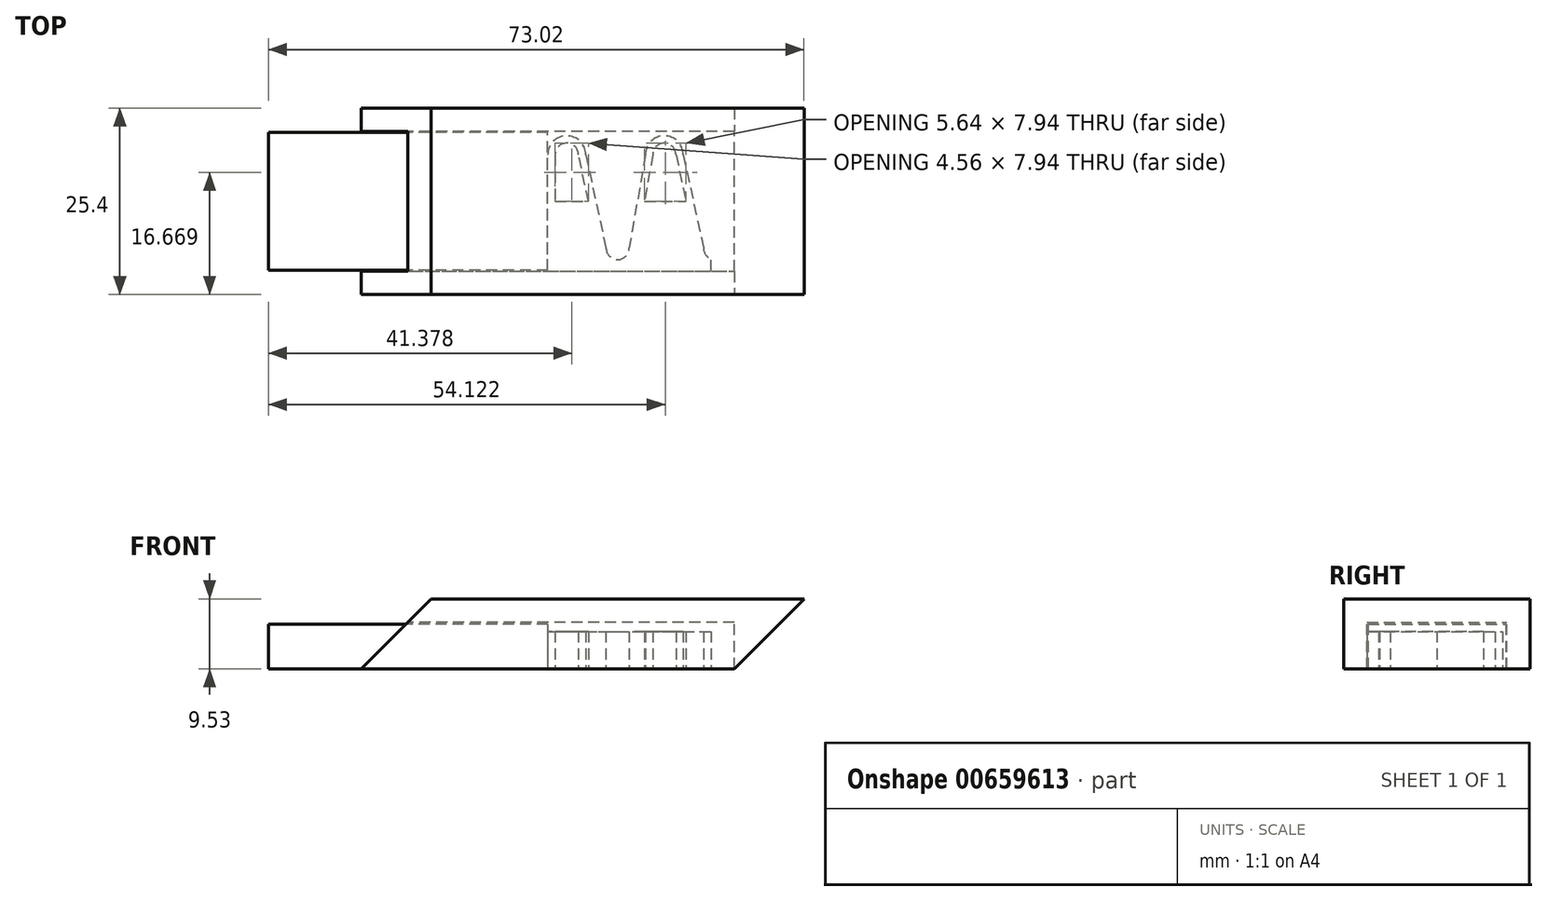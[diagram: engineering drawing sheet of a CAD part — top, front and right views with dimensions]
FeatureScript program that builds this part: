
annotation { "Feature Type Name" : "Feature", "Feature Type Description" : "" }
export const myFeature = defineFeature(function(context is Context, id is Id, definition is map)
    precondition{}
    {
        {
            var Q0;
            Q0=qCreatedBy(makeId("Top.planeOp"),FACE);
            var sketch = newSketch(context, id + "F0", { "sketchPlane" : qUnion([Q0])});
            skLineSegment(sketch, "E0.bottom", {"start": v(25.4, -12.7) * mm, "end": v(-25.4, -12.7) * mm});
            skLineSegment(sketch, "E0.top", {"start": v(25.4, 12.7) * mm, "end": v(-25.4, 12.7) * mm});
            skLineSegment(sketch, "E0.left", {"start": v(25.4, -12.7) * mm, "end": v(25.4, 12.7) * mm});
            skLineSegment(sketch, "E0.right", {"start": v(-25.4, -12.7) * mm, "end": v(-25.4, 12.7) * mm});
            skPoint(sketch, "E0.middle", {"position": v(0, 0) * mm});
            skLineSegment(sketch, "E1", {"start": v(25.4, 9.52) * mm, "end": v(-25.4, 9.52) * mm});
            skLineSegment(sketch, "E2", {"start": v(-25.4, -9.53) * mm, "end": v(25.4, -9.52) * mm});
            skSolve(sketch);
        }
        {
            var Q0;
            {var subQ0=sQuery(id+"F0.wireOp",EDGE,"E0.bottom");Q0=makeQuery(id+"F0.imprint","IMPRINT",FACE,{"disambiguationData":[TD([[makeQuery(id+"F0.imprint","IMPRINT",EDGE,{"derivedFrom":subQ0}),-1.0]])]});}
            var Q1;
            {var subQ0=sQuery(id+"F0.wireOp",EDGE,"E0.top");Q1=makeQuery(id+"F0.imprint","IMPRINT",FACE,{"disambiguationData":[TD([[makeQuery(id+"F0.imprint","IMPRINT",EDGE,{"derivedFrom":subQ0}),1.0]])]});}
            extrude(context, id + "F1", {"entities" : qUnion([Q0, Q1]), "depth" : 6.35 * mm, "offsetDistance" : 25.4 * mm});
        }
        {
            var Q0;
            Q0=makeQuery(id+"F1.opExtrude","SWEPT_FACE",FACE,{"disambiguationData":[OSD([sQuery(id+"F0.wireOp",EDGE,"E1")])]});
            var sketch = newSketch(context, id + "F2", { "sketchPlane" : qUnion([Q0])});
            skLineSegment(sketch, "E3.bottom", {"start": v(22.23, 6.35) * mm, "end": v(25.4, 6.35) * mm});
            skLineSegment(sketch, "E3.top", {"start": v(22.23, 0) * mm, "end": v(25.4, 0) * mm});
            skLineSegment(sketch, "E3.left", {"start": v(22.23, 6.35) * mm, "end": v(22.23, 0) * mm});
            skLineSegment(sketch, "E3.right", {"start": v(25.4, 6.35) * mm, "end": v(25.4, 0) * mm});
            skSolve(sketch);
        }
        {
            var Q0;
            Q0=makeQuery(id+"F2.imprint","IMPRINT",FACE,{"disambiguationData":[TD([[makeQuery(id+"F2.imprint","IMPRINT",EDGE,{"derivedFrom":sQuery(id+"F2.wireOp",EDGE,"E3.bottom")}),1.0]])]});
            extrude(context, id + "F3", {"entities" : qUnion([Q0]), "operationType" : NewBodyOperationType.ADD, "endBound" : BoundingType.UP_TO_NEXT, "depth" : 25.4 * mm, "offsetDistance" : 25.4 * mm});
        }
        {
            var Q0;
            Q0=qCreatedBy(makeId("Top.planeOp"),FACE);
            var sketch = newSketch(context, id + "F4", { "sketchPlane" : qUnion([Q0])});
            skLineSegment(sketch, "E4.bottom", {"start": v(-12.7, -9.4) * mm, "end": v(-38.1, -9.4) * mm});
            skLineSegment(sketch, "E4.top", {"start": v(-12.7, 9.4) * mm, "end": v(-38.1, 9.4) * mm});
            skLineSegment(sketch, "E4.left", {"start": v(-12.7, -9.4) * mm, "end": v(-12.7, 9.4) * mm});
            skLineSegment(sketch, "E4.right", {"start": v(-38.1, -9.4) * mm, "end": v(-38.1, 9.4) * mm});
            skPoint(sketch, "E4.middle", {"position": v(-25.4, 0) * mm});
            skSolve(sketch);
        }
        {
            var Q0;
            Q0 = qSketchRegion(id + "F4", true);
            extrude(context, id + "F5", {"entities" : qUnion([Q0]), "depth" : 6.1 * mm, "offsetDistance" : 25.4 * mm});
        }
        {
            var Q0;
            Q0=makeQuery(id+"F5.opExtrude","SWEPT_FACE",FACE,{"disambiguationData":[OSD([sQuery(id+"F4.wireOp",EDGE,"E4.left")])]});
            extrude(context, id + "F6", {"entities" : qUnion([Q0]), "operationType" : NewBodyOperationType.ADD, "depth" : 12.7 * mm, "offsetDistance" : 25.4 * mm});
        }
        {
            var Q0;
            {var subQ0=sQuery(id+"F0.wireOp",EDGE,"E0.right");Q0=makeQuery(id+"F1.opExtrude","CAP_EDGE",EDGE,{"disambiguationData":[OSD([subQ0]),TDD([makeQuery(id+"F0.imprint","IMPRINT",EDGE,{"disambiguationData":[TD([[makeQuery(id+"F0.imprint","INTERSECT",VERTEX,{"derivedFrom":[sQuery(id+"F0.wireOp",EDGE,"E0.bottom"),subQ0]}),-1.0]])],"derivedFrom":subQ0})])],"isStart":false});}
            var Q1;
            {var subQ0=sQuery(id+"F0.wireOp",EDGE,"E0.right");Q1=makeQuery(id+"F1.opExtrude","CAP_EDGE",EDGE,{"disambiguationData":[OSD([subQ0]),TDD([makeQuery(id+"F0.imprint","IMPRINT",EDGE,{"disambiguationData":[TD([[makeQuery(id+"F0.imprint","INTERSECT",VERTEX,{"derivedFrom":[sQuery(id+"F0.wireOp",EDGE,"E0.top"),subQ0]}),1.0]])],"derivedFrom":subQ0})])],"isStart":false});}
            chamfer(context, id + "F7", {"entities" : qUnion([Q0, Q1]), "width" : 6.35 * mm, "tangentPropagation" : true});
        }
        {
            var Q0;
            {var subQ0=sQuery(id+"F0.wireOp",EDGE,"E0.right");var subQ1=sQuery(id+"F0.wireOp",EDGE,"E0.left");Q0=makeQuery(id+"F3.boolean.opBoolean","MERGE",FACE,{"derivedFrom":[makeQuery(id+"F1.opExtrude","CAP_FACE",FACE,{"disambiguationData":[OSD([sQuery(id+"F0.wireOp",EDGE,"E0.bottom"),subQ1,subQ0,sQuery(id+"F0.wireOp",EDGE,"E2")])],"isStart":false}),makeQuery(id+"F1.opExtrude","CAP_FACE",FACE,{"disambiguationData":[OSD([sQuery(id+"F0.wireOp",EDGE,"E0.top"),subQ1,subQ0,sQuery(id+"F0.wireOp",EDGE,"E1")])],"isStart":false}),makeQuery(id+"F3.opExtrude","SWEPT_FACE",FACE,{"disambiguationData":[OSD([sQuery(id+"F2.wireOp",EDGE,"E3.bottom")])]})]});}
            var sketch = newSketch(context, id + "F8", { "sketchPlane" : qUnion([Q0])});
            skLineSegment(sketch, "E5.bottom", {"start": v(25.4, 12.7) * mm, "end": v(-19.05, 12.7) * mm});
            skLineSegment(sketch, "E5.top", {"start": v(25.4, -12.7) * mm, "end": v(-19.05, -12.7) * mm});
            skLineSegment(sketch, "E5.left", {"start": v(25.4, 12.7) * mm, "end": v(25.4, -12.7) * mm});
            skLineSegment(sketch, "E5.right", {"start": v(-19.05, 12.7) * mm, "end": v(-19.05, -12.7) * mm});
            skSolve(sketch);
        }
        {
            var Q0;
            Q0 = qSketchRegion(id + "F8", true);
            extrude(context, id + "F9", {"entities" : qUnion([Q0]), "operationType" : NewBodyOperationType.ADD, "depth" : 3.17 * mm, "offsetDistance" : 25.4 * mm});
        }
        {
            var Q0;
            Q0=makeQuery(id+"F9.opExtrude","CAP_EDGE",EDGE,{"disambiguationData":[OSD([sQuery(id+"F8.wireOp",EDGE,"E5.right")])],"isStart":false});
            chamfer(context, id + "F10", {"entities" : qUnion([Q0]), "width" : 3.17 * mm, "tangentPropagation" : true});
        }
        {
            var Q0;
            Q0=qCreatedBy(makeId("Top.planeOp"),FACE);
            var sketch = newSketch(context, id + "F11", { "sketchPlane" : qUnion([Q0])});
            skLineSegment(sketch, "E6.bottom", {"start": v(0, -9.53) * mm, "end": v(25.4, -9.53) * mm});
            skLineSegment(sketch, "E6.top", {"start": v(0, 9.53) * mm, "end": v(25.4, 9.53) * mm});
            skLineSegment(sketch, "E6.left", {"start": v(0, -9.53) * mm, "end": v(0, 9.53) * mm});
            skLineSegment(sketch, "E6.right", {"start": v(25.4, -9.52) * mm, "end": v(25.4, 9.53) * mm});
            skCircle(sketch, "E7", {"center": v(2.59, 6.35) * mm, "radius": 1.59 * mm});
            skCircle(sketch, "E8", {"center": v(9.53, -6.35) * mm, "radius": 1.59 * mm});
            skCircle(sketch, "E9", {"center": v(15.88, 6.35) * mm, "radius": 1.59 * mm});
            skCircle(sketch, "E10", {"center": v(22.81, -6.35) * mm, "radius": 1.59 * mm});
            skCircle(sketch, "E11", {"center": v(2.59, 6.35) * mm, "radius": 2.59 * mm});
            skCircle(sketch, "E12", {"center": v(9.53, -6.35) * mm, "radius": 2.59 * mm});
            skCircle(sketch, "E13", {"center": v(15.88, 6.35) * mm, "radius": 2.59 * mm});
            skCircle(sketch, "E14", {"center": v(22.81, -6.35) * mm, "radius": 2.59 * mm});
            skPoint(sketch, "E15", {"position": v(0, 0) * mm});
            skPoint(sketch, "E16", {"position": v(25.4, 0) * mm});
            skLineSegment(sketch, "E17", {"start": v(0, 0) * mm, "end": v(25.4, 0) * mm});
            skLineSegment(sketch, "E18", {"start": v(6.94, -6.35) * mm, "end": v(4.17, 6.35) * mm});
            skLineSegment(sketch, "E19", {"start": v(17.46, 6.35) * mm, "end": v(20.23, -6.35) * mm});
            skLineSegment(sketch, "E20", {"start": v(18.46, 6.35) * mm, "end": v(21.23, -6.35) * mm});
            skLineSegment(sketch, "E21", {"start": v(25.4, -6.35) * mm, "end": v(25.4, 9.53) * mm});
            skLineSegment(sketch, "E22", {"start": v(25.4, -6.35) * mm, "end": v(25.4, -6.35) * mm});
            skLineSegment(sketch, "E23", {"start": v(24.4, -6.35) * mm, "end": v(24.4, 9.53) * mm});
            skLineSegment(sketch, "E24", {"start": v(1, 6.35) * mm, "end": v(1, -9.53) * mm});
            skLineSegment(sketch, "E25", {"start": v(5.17, 6.35) * mm, "end": v(7.94, -6.35) * mm});
            skLineSegment(sketch, "E26", {"start": v(11.14, -6.35) * mm, "end": v(11.14, -6.35) * mm});
            skLineSegment(sketch, "E27", {"start": v(13.29, 6.35) * mm, "end": v(11.11, -6.35) * mm});
            skLineSegment(sketch, "E28", {"start": v(14.29, 6.35) * mm, "end": v(12.11, -6.35) * mm});
            skLineSegment(sketch, "E29", {"start": v(1, 0) * mm, "end": v(0, 0) * mm});
            skLineSegment(sketch, "E30", {"start": v(0, 0) * mm, "end": v(24.4, 0) * mm});
            skSolve(sketch);
        }
        {
            var Q0;
            {var subQ2=sQuery(id+"F11.wireOp",EDGE,"E18");var subQ4=sQuery(id+"F11.wireOp",EDGE,"E7");var subQ5=makeQuery(id+"F11.imprint","INTERSECT",VERTEX,{"derivedFrom":[subQ4,subQ2]});Q0=makeQuery(id+"F11.imprint","IMPRINT",FACE,{"disambiguationData":[TD([[makeQuery(id+"F11.imprint","IMPRINT",EDGE,{"disambiguationData":[TD([[subQ5,-1.0]])],"derivedFrom":subQ4}),-1.0]])]});}
            var Q1;
            {var subQ0=sQuery(id+"F11.wireOp",EDGE,"E25");var subQ1=sQuery(id+"F11.wireOp",EDGE,"E11");var subQ2=makeQuery(id+"F11.imprint","INTERSECT",VERTEX,{"derivedFrom":[subQ1,subQ0]});Q1=makeQuery(id+"F11.imprint","IMPRINT",FACE,{"disambiguationData":[TD([[makeQuery(id+"F11.imprint","IMPRINT",EDGE,{"disambiguationData":[TD([[subQ2,1.0]])],"derivedFrom":subQ1}),-1.0]])]});}
            var Q2;
            {var subQ0=sQuery(id+"F11.wireOp",EDGE,"E18");var subQ1=sQuery(id+"F11.wireOp",EDGE,"E12");var subQ2=makeQuery(id+"F11.imprint","INTERSECT",VERTEX,{"derivedFrom":[subQ1,subQ0]});Q2=makeQuery(id+"F11.imprint","IMPRINT",FACE,{"disambiguationData":[TD([[makeQuery(id+"F11.imprint","IMPRINT",EDGE,{"disambiguationData":[TD([[subQ2,1.0]])],"derivedFrom":subQ1}),-1.0]])]});}
            var Q3;
            {var subQ3=sQuery(id+"F11.wireOp",EDGE,"E25");var subQ5=sQuery(id+"F11.wireOp",EDGE,"E8");var subQ6=makeQuery(id+"F11.imprint","INTERSECT",VERTEX,{"derivedFrom":[subQ5,subQ3]});Q3=makeQuery(id+"F11.imprint","IMPRINT",FACE,{"disambiguationData":[TD([[makeQuery(id+"F11.imprint","IMPRINT",EDGE,{"disambiguationData":[TD([[subQ6,-1.0]])],"derivedFrom":subQ5}),-1.0]])]});}
            var Q4;
            {var subQ0=sQuery(id+"F11.wireOp",EDGE,"E28");var subQ1=sQuery(id+"F11.wireOp",EDGE,"E12");var subQ2=makeQuery(id+"F11.imprint","INTERSECT",VERTEX,{"derivedFrom":[subQ1,subQ0]});Q4=makeQuery(id+"F11.imprint","IMPRINT",FACE,{"disambiguationData":[TD([[makeQuery(id+"F11.imprint","IMPRINT",EDGE,{"disambiguationData":[TD([[subQ2,-1.0]])],"derivedFrom":subQ1}),-1.0]])]});}
            var Q5;
            {var subQ4=sQuery(id+"F11.wireOp",EDGE,"E9");var subQ7=sQuery(id+"F11.wireOp",EDGE,"E19");var subQ9=makeQuery(id+"F11.imprint","INTERSECT",VERTEX,{"derivedFrom":[subQ4,subQ7]});Q5=makeQuery(id+"F11.imprint","IMPRINT",FACE,{"disambiguationData":[TD([[makeQuery(id+"F11.imprint","IMPRINT",EDGE,{"disambiguationData":[TD([[subQ9,-1.0]])],"derivedFrom":subQ4}),-1.0]])]});}
            var Q6;
            {var subQ0=sQuery(id+"F11.wireOp",EDGE,"E20");var subQ1=sQuery(id+"F11.wireOp",EDGE,"E13");var subQ2=makeQuery(id+"F11.imprint","INTERSECT",VERTEX,{"derivedFrom":[subQ1,subQ0]});Q6=makeQuery(id+"F11.imprint","IMPRINT",FACE,{"disambiguationData":[TD([[makeQuery(id+"F11.imprint","IMPRINT",EDGE,{"disambiguationData":[TD([[subQ2,1.0]])],"derivedFrom":subQ1}),-1.0]])]});}
            var Q7;
            {var subQ5=sQuery(id+"F11.wireOp",EDGE,"E10");var subQ7=sQuery(id+"F11.wireOp",EDGE,"E20");var subQ9=makeQuery(id+"F11.imprint","INTERSECT",VERTEX,{"derivedFrom":[subQ5,subQ7]});Q7=makeQuery(id+"F11.imprint","IMPRINT",FACE,{"disambiguationData":[TD([[makeQuery(id+"F11.imprint","IMPRINT",EDGE,{"disambiguationData":[TD([[subQ9,-1.0]])],"derivedFrom":subQ5}),-1.0]])]});}
            var Q8;
            {var subQ0=sQuery(id+"F11.wireOp",EDGE,"E27");var subQ1=sQuery(id+"F11.wireOp",EDGE,"E13");var subQ2=makeQuery(id+"F11.imprint","INTERSECT",VERTEX,{"derivedFrom":[subQ1,subQ0]});Q8=makeQuery(id+"F11.imprint","IMPRINT",FACE,{"disambiguationData":[TD([[makeQuery(id+"F11.imprint","IMPRINT",EDGE,{"disambiguationData":[TD([[subQ2,-1.0]])],"derivedFrom":subQ1}),-1.0]])]});}
            var Q9;
            {var subQ0=sQuery(id+"F11.wireOp",EDGE,"E19");var subQ1=sQuery(id+"F11.wireOp",EDGE,"E14");var subQ2=makeQuery(id+"F11.imprint","INTERSECT",VERTEX,{"derivedFrom":[subQ1,subQ0]});Q9=makeQuery(id+"F11.imprint","IMPRINT",FACE,{"disambiguationData":[TD([[makeQuery(id+"F11.imprint","IMPRINT",EDGE,{"disambiguationData":[TD([[subQ2,1.0]])],"derivedFrom":subQ1}),-1.0]])]});}
            var Q10;
            {var subQ0=sQuery(id+"F11.wireOp",EDGE,"E30");var subQ1=sQuery(id+"F11.wireOp",EDGE,"E6.left");var subQ2=makeQuery(id+"F11.imprint","INTERSECT",VERTEX,{"derivedFrom":[subQ1,subQ0]});Q10=makeQuery(id+"F11.imprint","IMPRINT",FACE,{"disambiguationData":[TD([[makeQuery(id+"F11.imprint","IMPRINT",EDGE,{"disambiguationData":[TD([[subQ2,-1.0]])],"derivedFrom":subQ1}),-1.0]])]});}
            var Q11;
            {var subQ5=sQuery(id+"F11.wireOp",EDGE,"E17");Q11=makeQuery(id+"F11.imprint","IMPRINT",FACE,{"disambiguationData":[TD([[makeQuery(id+"F11.imprint","IMPRINT",EDGE,{"derivedFrom":subQ5}),-1.0]])]});}
            extrude(context, id + "F12", {"entities" : qUnion([Q0, Q1, Q2, Q3, Q4, Q5, Q6, Q7, Q8, Q9, Q10, Q11]), "depth" : 5.08 * mm, "offsetDistance" : 25.4 * mm});
        }
        {
            var Q0;
            {var subQ0=sQuery(id+"F0.wireOp",EDGE,"E0.right");var subQ1=sQuery(id+"F0.wireOp",EDGE,"E0.left");Q0=makeQuery(id+"F3.boolean.opBoolean","MERGE",FACE,{"derivedFrom":[makeQuery(id+"F1.opExtrude","CAP_FACE",FACE,{"disambiguationData":[OSD([sQuery(id+"F0.wireOp",EDGE,"E0.bottom"),subQ1,subQ0,sQuery(id+"F0.wireOp",EDGE,"E2")])],"isStart":true}),makeQuery(id+"F1.opExtrude","CAP_FACE",FACE,{"disambiguationData":[OSD([sQuery(id+"F0.wireOp",EDGE,"E0.top"),subQ1,subQ0,sQuery(id+"F0.wireOp",EDGE,"E1")])],"isStart":true}),makeQuery(id+"F3.opExtrude","SWEPT_FACE",FACE,{"disambiguationData":[OSD([sQuery(id+"F2.wireOp",EDGE,"E3.top")])]})]});}
            var sketch = newSketch(context, id + "F13", { "sketchPlane" : qUnion([Q0])});
            skLineSegment(sketch, "E31.bottom", {"start": v(22.23, 9.52) * mm, "end": v(25.4, 9.52) * mm});
            skLineSegment(sketch, "E31.top", {"start": v(22.23, -9.52) * mm, "end": v(25.4, -9.52) * mm});
            skLineSegment(sketch, "E31.left", {"start": v(22.23, 9.52) * mm, "end": v(22.23, -9.52) * mm});
            skLineSegment(sketch, "E31.right", {"start": v(25.4, 9.52) * mm, "end": v(25.4, -9.52) * mm});
            skSolve(sketch);
        }
        {
            var Q0;
            Q0=makeQuery(id+"F13.imprint","IMPRINT",FACE,{"disambiguationData":[TD([[makeQuery(id+"F13.imprint","IMPRINT",EDGE,{"derivedFrom":sQuery(id+"F13.wireOp",EDGE,"E31.bottom")}),-1.0]])]});
            extrude(context, id + "F14", {"entities" : qUnion([Q0]), "operationType" : NewBodyOperationType.REMOVE, "oppositeDirection" : true, "depth" : 6.35 * mm, "offsetDistance" : 25.4 * mm});
        }
        {
            var Q0;
            {var subQ0=sQuery(id+"F0.wireOp",EDGE,"E0.left");Q0=makeQuery(id+"F9.boolean.opBoolean","MERGE",FACE,{"derivedFrom":[makeQuery(id+"F3.boolean.opBoolean","MERGE",FACE,{"derivedFrom":[makeQuery(id+"F1.opExtrude","SWEPT_FACE",FACE,{"disambiguationData":[OSD([subQ0]),TDD([makeQuery(id+"F0.imprint","IMPRINT",EDGE,{"disambiguationData":[TD([[makeQuery(id+"F0.imprint","INTERSECT",VERTEX,{"derivedFrom":[sQuery(id+"F0.wireOp",EDGE,"E0.bottom"),subQ0]}),-1.0]])],"derivedFrom":subQ0})])]}),makeQuery(id+"F1.opExtrude","SWEPT_FACE",FACE,{"disambiguationData":[OSD([subQ0]),TDD([makeQuery(id+"F0.imprint","IMPRINT",EDGE,{"disambiguationData":[TD([[makeQuery(id+"F0.imprint","INTERSECT",VERTEX,{"derivedFrom":[sQuery(id+"F0.wireOp",EDGE,"E0.top"),subQ0]}),1.0]])],"derivedFrom":subQ0})])]}),makeQuery(id+"F3.opExtrude","SWEPT_FACE",FACE,{"disambiguationData":[OSD([sQuery(id+"F2.wireOp",EDGE,"E3.right")])]})]}),makeQuery(id+"F9.opExtrude","SWEPT_FACE",FACE,{"disambiguationData":[OSD([sQuery(id+"F8.wireOp",EDGE,"E5.left")])]})]});}
            extrude(context, id + "F15", {"entities" : qUnion([Q0]), "operationType" : NewBodyOperationType.ADD, "depth" : 9.52 * mm, "offsetDistance" : 25.4 * mm});
        }
        {
            var Q0;
            {var subQ0=sQuery(id+"F13.wireOp",EDGE,"E31.right");Q0=makeQuery(id+"F15.boolean.opBoolean","MERGE",FACE,{"derivedFrom":[makeQuery(id+"F14.boolean.opBoolean","MERGE",FACE,{"derivedFrom":[makeQuery(id+"F9.opExtrude","CAP_FACE",FACE,{"disambiguationData":[OSD([sQuery(id+"F8.wireOp",EDGE,"E5.bottom"),sQuery(id+"F8.wireOp",EDGE,"E5.top"),sQuery(id+"F8.wireOp",EDGE,"E5.left"),sQuery(id+"F8.wireOp",EDGE,"E5.right")])],"isStart":true}),makeQuery(id+"F14.opExtrude","CAP_FACE",FACE,{"disambiguationData":[OSD([sQuery(id+"F13.wireOp",EDGE,"E31.bottom"),sQuery(id+"F13.wireOp",EDGE,"E31.top"),sQuery(id+"F13.wireOp",EDGE,"E31.left"),subQ0])],"isStart":false})]}),makeQuery(id+"F15.opExtrude","SWEPT_FACE",FACE,{"disambiguationData":[OSD([subQ0])]})]});}
            var sketch = newSketch(context, id + "F16", { "sketchPlane" : qUnion([Q0])});
            skLineSegment(sketch, "E32.bottom", {"start": v(34.93, 9.52) * mm, "end": v(25.4, 9.52) * mm});
            skLineSegment(sketch, "E32.top", {"start": v(34.93, -9.52) * mm, "end": v(25.4, -9.52) * mm});
            skLineSegment(sketch, "E32.left", {"start": v(34.93, 9.52) * mm, "end": v(34.93, -9.52) * mm});
            skLineSegment(sketch, "E32.right", {"start": v(25.4, 9.52) * mm, "end": v(25.4, -9.52) * mm});
            skSolve(sketch);
        }
        {
            var Q0;
            Q0 = qSketchRegion(id + "F16", true);
            extrude(context, id + "F17", {"entities" : qUnion([Q0]), "operationType" : NewBodyOperationType.ADD, "depth" : 6.35 * mm, "offsetDistance" : 25.4 * mm});
        }
        {
            var Q0;
            {var subQ1=sQuery(id+"F2.wireOp",EDGE,"E3.top");var subQ3=sQuery(id+"F2.wireOp",EDGE,"E3.right");var subQ6=sQuery(id+"F0.wireOp",EDGE,"E0.left");var subQ7=sQuery(id+"F0.wireOp",EDGE,"E0.top");var subQ8=makeQuery(id+"F0.imprint","IMPRINT",EDGE,{"disambiguationData":[TD([[makeQuery(id+"F0.imprint","INTERSECT",VERTEX,{"derivedFrom":[subQ7,subQ6]}),1.0]])],"derivedFrom":subQ6});var subQ12=sQuery(id+"F0.wireOp",EDGE,"E0.bottom");var subQ14=makeQuery(id+"F0.imprint","IMPRINT",EDGE,{"disambiguationData":[TD([[makeQuery(id+"F0.imprint","INTERSECT",VERTEX,{"derivedFrom":[subQ12,subQ6]}),-1.0]])],"derivedFrom":subQ6});var subQ17=makeQuery(id+"F3.boolean.opBoolean","MERGE",EDGE,{"derivedFrom":[makeQuery(id+"F1.opExtrude","CAP_EDGE",EDGE,{"disambiguationData":[OSD([subQ6]),TDD([subQ14])],"isStart":true}),makeQuery(id+"F1.opExtrude","CAP_EDGE",EDGE,{"disambiguationData":[OSD([subQ6]),TDD([subQ8])],"isStart":true}),makeQuery(id+"F3.opExtrude","SWEPT_EDGE",EDGE,{"disambiguationData":[OSD([subQ1,subQ3])]})]});Q0=makeQuery(id+"F17.boolean.opBoolean","MERGE",EDGE,{"derivedFrom":[makeQuery(id+"F15.opExtrude","CAP_EDGE",EDGE,{"disambiguationData":[OSD([subQ6,subQ1,subQ3]),TDD([makeQuery(id+"F14.boolean.opBoolean","SPLIT",EDGE,{"disambiguationData":[TD([makeQuery(id+"F1.opExtrude","SWEPT_FACE",FACE,{"disambiguationData":[OSD([subQ12])]})])],"derivedFrom":subQ17})])],"isStart":false}),makeQuery(id+"F15.opExtrude","CAP_EDGE",EDGE,{"disambiguationData":[OSD([subQ6,subQ1,subQ3]),TDD([makeQuery(id+"F14.boolean.opBoolean","SPLIT",EDGE,{"disambiguationData":[TD([makeQuery(id+"F1.opExtrude","SWEPT_FACE",FACE,{"disambiguationData":[OSD([subQ7])]})])],"derivedFrom":subQ17})])],"isStart":false}),makeQuery(id+"F17.opExtrude","CAP_EDGE",EDGE,{"disambiguationData":[OSD([sQuery(id+"F16.wireOp",EDGE,"E32.left")])],"isStart":false})]});}
            chamfer(context, id + "F18", {"entities" : qUnion([Q0]), "width" : 9.52 * mm, "tangentPropagation" : true});
        }
    });
